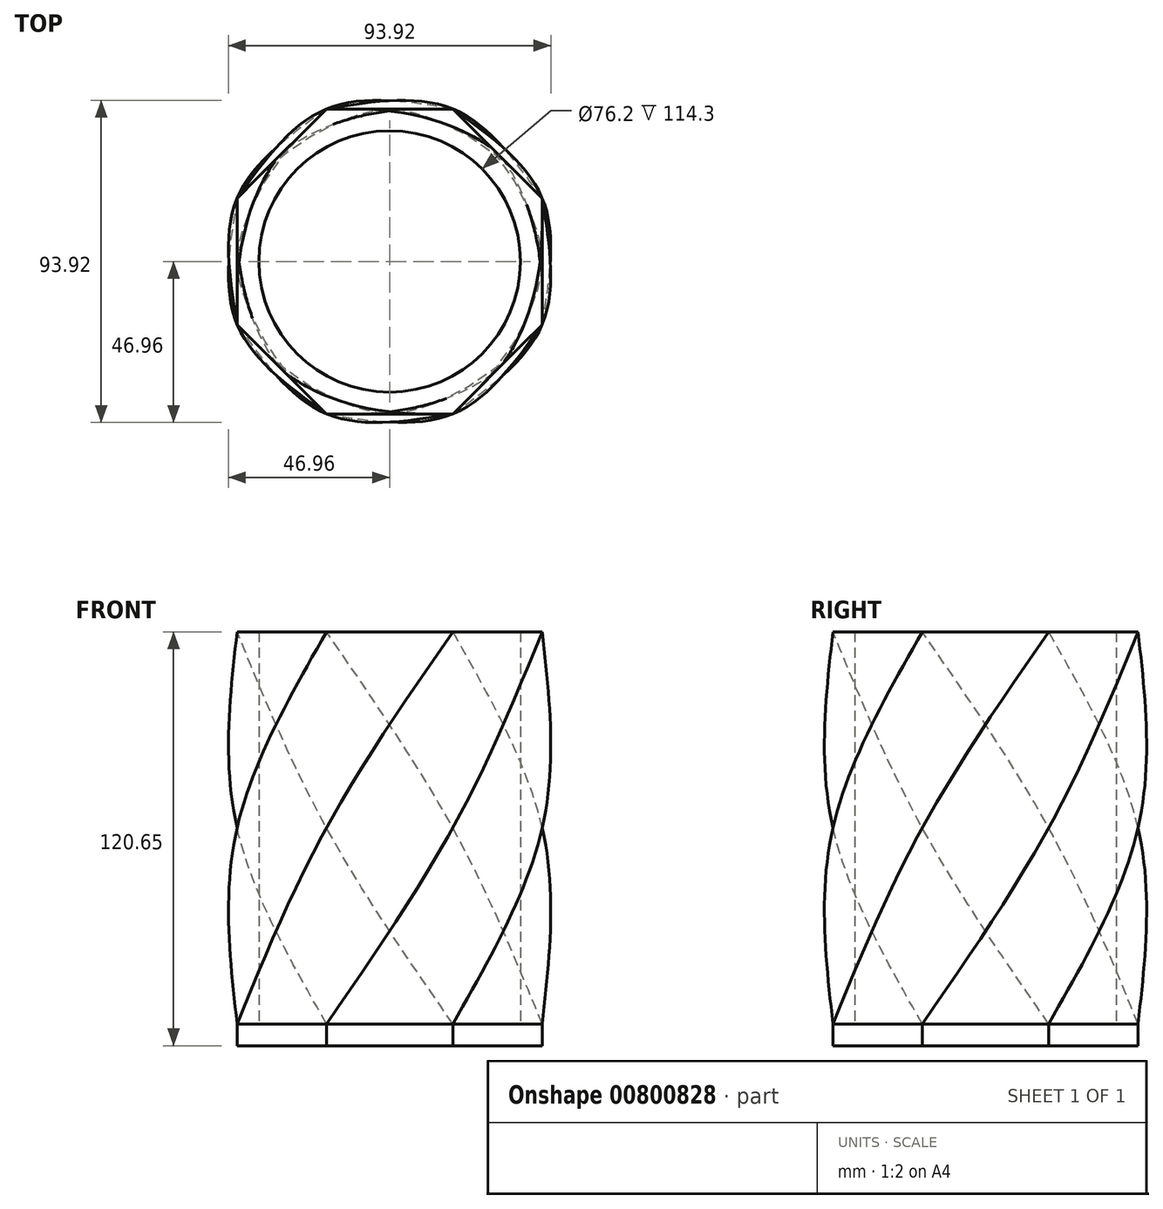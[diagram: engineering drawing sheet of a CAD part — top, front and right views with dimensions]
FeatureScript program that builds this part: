
annotation { "Feature Type Name" : "Feature", "Feature Type Description" : "" }
export const myFeature = defineFeature(function(context is Context, id is Id, definition is map)
    precondition{}
    {
        {
            var Q0;
            Q0=qCreatedBy(makeId("Top.planeOp"),FACE);
            var sketch = newSketch(context, id + "F0", { "sketchPlane" : qUnion([Q0])});
            skCircle(sketch, "E0", {"center": v(0, 0) * mm, "radius": 38.1 * mm});
            skCircle(sketch, "E1.cCircle", {"center": v(0, 0) * mm, "radius": 44.45 * mm, "construction": true});
            skLineSegment(sketch, "E1.0", {"start": v(-18.41, 44.45) * mm, "end": v(18.41, 44.45) * mm});
            skLineSegment(sketch, "E1.1", {"start": v(18.41, 44.45) * mm, "end": v(44.45, 18.41) * mm});
            skLineSegment(sketch, "E1.2", {"start": v(44.45, 18.41) * mm, "end": v(44.45, -18.41) * mm});
            skLineSegment(sketch, "E1.3", {"start": v(44.45, -18.41) * mm, "end": v(18.41, -44.45) * mm});
            skLineSegment(sketch, "E1.4", {"start": v(18.41, -44.45) * mm, "end": v(-18.41, -44.45) * mm});
            skLineSegment(sketch, "E1.5", {"start": v(-18.41, -44.45) * mm, "end": v(-44.45, -18.41) * mm});
            skLineSegment(sketch, "E1.6", {"start": v(-44.45, -18.41) * mm, "end": v(-44.45, 18.41) * mm});
            skLineSegment(sketch, "E1.7", {"start": v(-44.45, 18.41) * mm, "end": v(-18.41, 44.45) * mm});
            skPoint(sketch, "E1.0.midPoint", {"position": v(0, 44.45) * mm});
            skLineSegment(sketch, "E2", {"start": v(-38.1, 0) * mm, "end": v(0, 0) * mm});
            skLineSegment(sketch, "E3", {"start": v(-38.1, 0) * mm, "end": v(-44.45, 0) * mm, "construction": true});
            skLineSegment(sketch, "E4", {"start": v(0, 0) * mm, "end": v(0, 38.1) * mm});
            skLineSegment(sketch, "E5", {"start": v(0, 0) * mm, "end": v(38.1, 0) * mm});
            skSolve(sketch);
        }
        {
            var Q0;
            {var subQ0=sQuery(id+"F0.wireOp",EDGE,"E2");Q0=makeQuery(id+"F0.imprint","IMPRINT",FACE,{"disambiguationData":[TD([[makeQuery(id+"F0.imprint","IMPRINT",EDGE,{"derivedFrom":subQ0}),1.0]])]});}
            extrude(context, id + "F1", {"entities" : qUnion([Q0]), "depth" : 114.3 * mm, "offsetDistance" : 25.4 * mm});
        }
        {
            var Q0;
            Q0=qCreatedBy(makeId("Top.planeOp"),FACE);
            var sketch = newSketch(context, id + "F2", { "sketchPlane" : qUnion([Q0])});
            skCircle(sketch, "E6.cCircle", {"center": v(0, 0) * mm, "radius": 44.45 * mm, "construction": true});
            skLineSegment(sketch, "E6.0", {"start": v(-18.41, -44.45) * mm, "end": v(-44.45, -18.41) * mm});
            skLineSegment(sketch, "E6.1", {"start": v(-44.45, -18.41) * mm, "end": v(-44.45, 18.41) * mm});
            skLineSegment(sketch, "E6.2", {"start": v(-44.45, 18.41) * mm, "end": v(-18.41, 44.45) * mm});
            skLineSegment(sketch, "E6.3", {"start": v(-18.41, 44.45) * mm, "end": v(18.41, 44.45) * mm});
            skLineSegment(sketch, "E6.4", {"start": v(18.41, 44.45) * mm, "end": v(44.45, 18.41) * mm});
            skLineSegment(sketch, "E6.5", {"start": v(44.45, 18.41) * mm, "end": v(44.45, -18.41) * mm});
            skLineSegment(sketch, "E6.6", {"start": v(44.45, -18.41) * mm, "end": v(18.41, -44.45) * mm});
            skLineSegment(sketch, "E6.7", {"start": v(18.41, -44.45) * mm, "end": v(-18.41, -44.45) * mm});
            skPoint(sketch, "E6.0.midPoint", {"position": v(-31.43, -31.43) * mm});
            skSolve(sketch);
        }
        {
            var Q0;
            Q0=qCreatedBy(makeId("Front.planeOp"),FACE);
            var sketch = newSketch(context, id + "F3", { "sketchPlane" : qUnion([Q0])});
            skLineSegment(sketch, "E7.0", {"start": v(18.41, 0) * mm, "end": v(-18.41, 0) * mm});
            skLineSegment(sketch, "E8", {"start": v(18.41, 0) * mm, "end": v(18.41, 57.15) * mm});
            skLineSegment(sketch, "E9", {"start": v(18.41, 57.15) * mm, "end": v(18.41, 114.3) * mm});
            skLineSegment(sketch, "E10", {"start": v(18.41, 114.3) * mm, "end": v(-18.41, 0) * mm});
            skPoint(sketch, "E11.0", {"position": v(0, 114.3) * mm});
            skSolve(sketch);
        }
        {
            var Q0;
            Q0=sQuery(id+"F3.wireOp",VERTEX,"E10.start");
            var Q1;
            Q1=sQuery(id+"F3.wireOp",VERTEX,"E7.0.start");
            cPlane(context, id + "F4", {"entities" : qUnion([Q0, Q1]), "cplaneType" : CPlaneType.MID_PLANE, "offset" : 25.4 * mm, "width" : 152.4 * mm, "height" : 152.4 * mm});
        }
        {
            var Q0;
            Q0=sQuery(id+"F3.wireOp",VERTEX,"E10.start");
            var Q1;
            Q1=sQuery(id+"F3.wireOp",EDGE,"E9");
            cPlane(context, id + "F5", {"entities" : qUnion([Q0, Q1]), "cplaneType" : CPlaneType.LINE_POINT, "offset" : 25.4 * mm, "width" : 152.4 * mm, "height" : 152.4 * mm});
        }
        {
            var Q0;
            Q0=qCreatedBy(id+"F4.planeOp",FACE);
            var sketch = newSketch(context, id + "F6", { "sketchPlane" : qUnion([Q0])});
            skCircle(sketch, "E12.cCircle", {"center": v(0, 0) * mm, "radius": 44.45 * mm, "construction": true});
            skLineSegment(sketch, "E12.0", {"start": v(-18.41, -44.45) * mm, "end": v(-44.45, -18.41) * mm});
            skLineSegment(sketch, "E12.1", {"start": v(-44.45, -18.41) * mm, "end": v(-44.45, 18.41) * mm});
            skLineSegment(sketch, "E12.2", {"start": v(-44.45, 18.41) * mm, "end": v(-18.41, 44.45) * mm});
            skLineSegment(sketch, "E12.3", {"start": v(-18.41, 44.45) * mm, "end": v(18.41, 44.45) * mm});
            skLineSegment(sketch, "E12.4", {"start": v(18.41, 44.45) * mm, "end": v(44.45, 18.41) * mm});
            skLineSegment(sketch, "E12.5", {"start": v(44.45, 18.41) * mm, "end": v(44.45, -18.41) * mm});
            skLineSegment(sketch, "E12.6", {"start": v(44.45, -18.41) * mm, "end": v(18.41, -44.45) * mm});
            skLineSegment(sketch, "E12.7", {"start": v(18.41, -44.45) * mm, "end": v(-18.41, -44.45) * mm});
            skPoint(sketch, "E12.0.midPoint", {"position": v(-31.43, -31.43) * mm});
            skSolve(sketch);
        }
        {
            var Q0;
            Q0=qCreatedBy(id+"F5.planeOp",FACE);
            var sketch = newSketch(context, id + "F7", { "sketchPlane" : qUnion([Q0])});
            skCircle(sketch, "E13.cCircle", {"center": v(0, 0) * mm, "radius": 44.45 * mm, "construction": true});
            skLineSegment(sketch, "E13.0", {"start": v(-18.41, -44.45) * mm, "end": v(-44.45, -18.41) * mm});
            skLineSegment(sketch, "E13.1", {"start": v(-44.45, -18.41) * mm, "end": v(-44.45, 18.41) * mm});
            skLineSegment(sketch, "E13.2", {"start": v(-44.45, 18.41) * mm, "end": v(-18.41, 44.45) * mm});
            skLineSegment(sketch, "E13.3", {"start": v(-18.41, 44.45) * mm, "end": v(18.41, 44.45) * mm});
            skLineSegment(sketch, "E13.4", {"start": v(18.41, 44.45) * mm, "end": v(44.45, 18.41) * mm});
            skLineSegment(sketch, "E13.5", {"start": v(44.45, 18.41) * mm, "end": v(44.45, -18.41) * mm});
            skLineSegment(sketch, "E13.6", {"start": v(44.45, -18.41) * mm, "end": v(18.41, -44.45) * mm});
            skLineSegment(sketch, "E13.7", {"start": v(18.41, -44.45) * mm, "end": v(-18.41, -44.45) * mm});
            skPoint(sketch, "E13.0.midPoint", {"position": v(-31.43, -31.43) * mm});
            skSolve(sketch);
        }
        {
            var Q1;
            Q1=makeQuery(id+"F2.imprint","IMPRINT",FACE,{"disambiguationData":[TD([[makeQuery(id+"F2.imprint","IMPRINT",EDGE,{"derivedFrom":sQuery(id+"F2.wireOp",EDGE,"E6.0")}),-1.0]])]});
            var Q2;
            Q2=makeQuery(id+"F6.imprint","IMPRINT",FACE,{"disambiguationData":[TD([[makeQuery(id+"F6.imprint","IMPRINT",EDGE,{"derivedFrom":sQuery(id+"F6.wireOp",EDGE,"E12.0")}),-1.0]])]});
            var Q3;
            Q3=makeQuery(id+"F7.imprint","IMPRINT",FACE,{"disambiguationData":[TD([[makeQuery(id+"F7.imprint","IMPRINT",EDGE,{"derivedFrom":sQuery(id+"F7.wireOp",EDGE,"E13.0")}),-1.0]])]});
            var Q4;
            Q4=sQuery(id+"F2.wireOp",VERTEX,"E6.7.end");
            var Q5;
            Q5=sQuery(id+"F6.wireOp",VERTEX,"E12.4.start");
            var Q6;
            Q6=sQuery(id+"F7.wireOp",VERTEX,"E13.6.start");
            loft(context, id + "F8", {"sheetProfilesArray" : [{ "sheetProfileEntities" : qUnion([Q1]) }, { "sheetProfileEntities" : qUnion([Q2]) }, { "sheetProfileEntities" : qUnion([Q3]) }], "matchConnections" : true, "connections" : [{ "connectionEntities" : qUnion([Q4, Q5, Q6]), "connectionEdgeQueries" : qUnion([]), "connectionEdgeParameters" : [] }]});
        }
        {
            var Q0;
            Q0=makeQuery(id+"F1.opExtrude","SWEPT_BODY",BODY,{"disambiguationData":[OSD([sQuery(id+"F0.wireOp",EDGE,"E0"),sQuery(id+"F0.wireOp",EDGE,"E2"),sQuery(id+"F0.wireOp",EDGE,"E4")])]});
            deleteBodies(context, id + "F9", {"entities" : qUnion([Q0])});
        }
        {
            var Q0;
            Q0=qCreatedBy(makeId("Top.planeOp"),FACE);
            var sketch = newSketch(context, id + "F10", { "sketchPlane" : qUnion([Q0])});
            skCircle(sketch, "E14", {"center": v(0, 0) * mm, "radius": 38.1 * mm});
            skSolve(sketch);
        }
        {
            var Q0;
            Q0=qSketchRegion(id+"F10",true);
            extrude(context, id + "F11", {"entities" : qUnion([Q0]), "operationType" : NewBodyOperationType.REMOVE, "depth" : 114.3 * mm, "offsetDistance" : 25.4 * mm});
        }
        {
            var Q0;
            Q0=makeQuery(id+"F2.imprint","IMPRINT",FACE,{"disambiguationData":[TD([[makeQuery(id+"F2.imprint","IMPRINT",EDGE,{"derivedFrom":sQuery(id+"F2.wireOp",EDGE,"E6.0")}),-1.0]])]});
            extrude(context, id + "F12", {"entities" : qUnion([Q0]), "operationType" : NewBodyOperationType.ADD, "oppositeDirection" : true, "depth" : 6.35 * mm, "offsetDistance" : 25.4 * mm});
        }
    });
